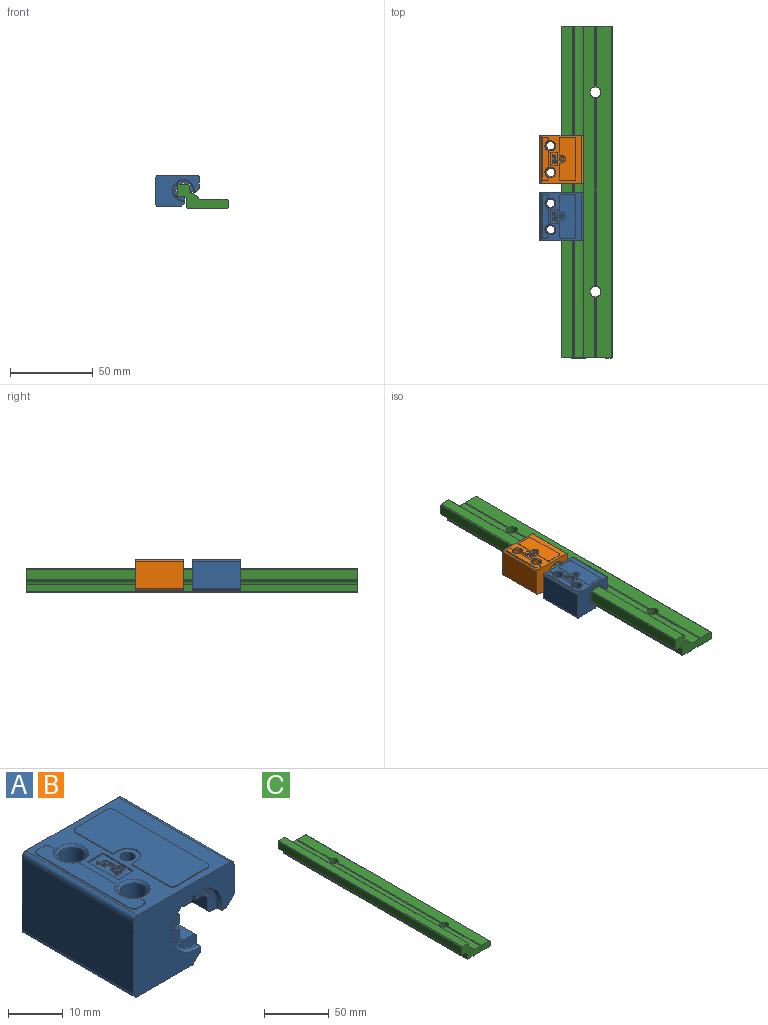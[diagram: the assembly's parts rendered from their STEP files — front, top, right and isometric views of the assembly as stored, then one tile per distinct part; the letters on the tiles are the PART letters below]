
ASSEMBLY  parts=3 mates=2
PART A: 216 faces, bbox 26.3x29.3x18.8 mm
  f0: plane 0.15x0.14mm, normal (0,0,1), area 0mm2, adj f1,f2,f3,f4
  f1: plane 0.15x0.15mm, normal (0,1,0), area 0mm2, adj f0,f2,f4,f5
  f2: plane 0.15x0.06mm, normal (1,0,0), area 0mm2, adj f0,f1,f3,f5
  f3: cylinder r=0.07mm len=0.15mm, axis (0,0,1), area 0mm2, adj f0,f2,f4,f5
  f4: plane 0.15x0.06mm, normal (-1,0,0), area 0mm2, adj f0,f1,f3,f5
  f5: plane 0.35x0.16mm, normal (0,0,1), area 0mm2, adj f1,f2,f3,f4,f6,f7,f8,f9
  f6: plane 0.18x0.15mm, normal (0,1,0), area 0mm2, adj f5,f7,f15,f16
  f7: plane 0.15x0.01mm, normal (1,0,0), area 0mm2, adj f5,f6,f8,f16
  f8: plane 0.35x0.15mm, normal (0,-1,0), area 0.1mm2, adj f5,f7,f9,f16
  f9: plane 0.15x0.08mm, normal (-1,0,0), area 0mm2, adj f5,f8,f10,f16
  f10: cylinder r=0.09mm len=0.18mm, axis (0,0,-1), area 0mm2, adj f5,f9,f11,f16
  f11: plane 0.15x0.01mm, normal (1,0,0), area 0mm2, adj f5,f10,f12,f16
  f12: plane 0.18x0.15mm, normal (-0.5,0.87,0), area 0mm2, adj f5,f11,f13,f16
  f13: plane 0.15x0.01mm, normal (1,0,0), area 0mm2, adj f5,f12,f14,f16
  f14: plane 0.18x0.15mm, normal (0.5,-0.87,0), area 0mm2, adj f5,f13,f15,f16
  f15: plane 0.15x0.04mm, normal (1,0,0), area 0mm2, adj f5,f6,f14,f16
  f16: plane 0.51x0.51mm, normal (0,0,1), area 0.2mm2, adj f6,f7,f8,f9,f10,f11,f12,f13
  f17: plane 1.38x0.63mm, normal (0,0,1), area 0.6mm2, adj f21,f22
  f18: plane 1.36x0.62mm, normal (0,0,1), area 0.6mm2, adj f23,f24
  f19: plane 1.37x0.74mm, normal (0,0,1), area 0.8mm2, adj f25,f26
  f20: cylinder r=0.25mm len=0.5mm, axis (0,0,1), area 0.2mm2, adj f16,f59
  f21: cylinder r=0.68mm len=1.35mm, axis (0,0,1), area 0.3mm2, adj f17,f22,f60
  f22: plane 1.35x0.15mm, normal (1,0,0), area 0.2mm2, adj f17,f21,f60
  f23: cylinder r=0.68mm len=1.34mm, axis (0,0,1), area 0.3mm2, adj f18,f24,f60
  f24: plane 1.34x0.15mm, normal (1,0,0), area 0.2mm2, adj f18,f23,f60
  f25: plane 1.35x0.15mm, normal (-1,0,0), area 0.2mm2, adj f19,f26,f60
  f26: cylinder r=0.68mm len=1.35mm, axis (0,0,1), area 0.3mm2, adj f19,f25,f60
  f27: plane 0.35x0.15mm, normal (0,1,0), area 0mm2, adj f29,f74,f79
  f28: plane 0.35x0.15mm, normal (0,-1,0), area 0mm2, adj f30,f74,f80
  f29: cylinder r=6mm len=12mm, axis (0,1,0), area 4.1mm2, adj f27,f74,f79,f85
  f30: cylinder r=6mm len=12mm, axis (0,1,0), area 4.1mm2, adj f28,f74,f80,f87
  f31: plane 27x2.99mm, normal (0,0,1), area 80.7mm2, adj f32,f85,f86,f87
  f32: plane 27x0.46mm, normal (-0.71,0,0.71), area 17.5mm2, adj f31,f33,f85,f87
  f33: cylinder r=0.3mm len=27mm, axis (0,-1,0), area 12.7mm2, adj f32,f34,f85,f87
  f34: plane 27x0.64mm, normal (0.71,0,0.71), area 24.3mm2, adj f33,f35,f85,f87
  f35: cylinder r=0.3mm len=27mm, axis (0,-1,0), area 12.7mm2, adj f34,f36,f85,f87
  f36: plane 27x0.46mm, normal (0.71,0,-0.71), area 17.5mm2, adj f35,f37,f85,f87
  f37: plane 27x2.19mm, normal (1,0,0), area 59.1mm2, adj f36,f38,f85,f87
  f38: plane 27x0.75mm, normal (0,0,1), area 20.2mm2, adj f37,f39,f85,f87
  f39: cylinder r=0.5mm len=27mm, axis (0,-1,0), area 42.4mm2, adj f38,f40,f85,f87
  f40: plane 27x0.75mm, normal (0,0,-1), area 20.2mm2, adj f39,f41,f85,f87
  f41: plane 27x2.19mm, normal (1,0,0), area 59.1mm2, adj f40,f42,f85,f87
  f42: plane 27x0.46mm, normal (0.71,0,0.71), area 17.5mm2, adj f41,f43,f85,f87
  f43: cylinder r=0.3mm len=27mm, axis (0,-1,0), area 12.7mm2, adj f42,f44,f85,f87
  f44: plane 27x0.64mm, normal (0.71,0,-0.71), area 24.3mm2, adj f43,f45,f85,f87
  f45: cylinder r=0.3mm len=27mm, axis (0,-1,0), area 12.7mm2, adj f44,f46,f85,f87
  f46: plane 27x0.46mm, normal (-0.71,0,-0.71), area 17.5mm2, adj f45,f47,f85,f87
  f47: plane 27x2.19mm, normal (0,0,-1), area 59.1mm2, adj f46,f48,f85,f87
  f48: plane 27x0.75mm, normal (1,0,0), area 20.2mm2, adj f47,f49,f85,f87
  f49: cylinder r=0.5mm len=27mm, axis (0,-1,0), area 42.4mm2, adj f48,f50,f85,f87
  f50: plane 27x0.75mm, normal (-1,0,0), area 20.2mm2, adj f49,f51,f85,f87
  f51: plane 27x2.19mm, normal (0,0,-1), area 59.1mm2, adj f50,f52,f85,f87
  f52: plane 27x0.46mm, normal (0.71,0,-0.71), area 17.5mm2, adj f51,f53,f85,f87
  f53: cylinder r=0.3mm len=27mm, axis (0,-1,0), area 12.7mm2, adj f52,f54,f85,f87
  f54: plane 27x0.64mm, normal (-0.71,0,-0.71), area 24.3mm2, adj f53,f55,f85,f87
  f55: cylinder r=0.3mm len=27mm, axis (0,-1,0), area 12.7mm2, adj f54,f56,f85,f87
  f56: plane 27x0.46mm, normal (-0.71,0,0.71), area 17.5mm2, adj f55,f57,f85,f87
  f57: plane 27x2.99mm, normal (-1,0,0), area 80.7mm2, adj f56,f58,f85,f87
  f58: plane 27x0.5mm, normal (-0.71,0,-0.71), area 19.1mm2, adj f57,f74,f85,f87
  f59: plane 0.56x0.56mm, normal (0,0,1), area 0mm2, adj f20,f91
  f60: plane 5.04x2.57mm, normal (0,0,1), area 3.1mm2, adj f21,f22,f23,f24,f25,f26,f92,f93
  f61: plane 0.2x0.2mm, normal (0,0,1), area 0mm2, adj f149
  f62: plane 3x0.5mm, normal (-0.71,0,0.71), area 2.1mm2, adj f63,f90,f150,f151
  f63: cylinder r=6mm len=3mm, axis (0,1,0), area 4.5mm2, adj f62,f64,f150,f151
  f64: plane 3x0.5mm, normal (0.71,0,-0.71), area 2.1mm2, adj f63,f65,f150,f151
  f65: cylinder r=6.7mm len=8.36mm, axis (0,1,0), area 27.1mm2, adj f64,f66,f150,f151
  f66: plane 3x0.5mm, normal (0.71,0,0.71), area 2.1mm2, adj f65,f67,f150,f151
  f67: cylinder r=6mm len=3mm, axis (0,1,0), area 4.5mm2, adj f66,f68,f150,f151
  f68: plane 3x0.5mm, normal (-0.71,0,-0.71), area 2.1mm2, adj f67,f69,f150,f151
  f69: cylinder r=6.7mm len=8.36mm, axis (0,1,0), area 27.1mm2, adj f68,f70,f150,f151
  f70: plane 3x0.5mm, normal (0.71,0,-0.71), area 2.1mm2, adj f69,f71,f150,f151
  f71: cylinder r=6mm len=3mm, axis (0,1,0), area 4.5mm2, adj f70,f72,f150,f151
  f72: plane 3x0.5mm, normal (-0.71,0,0.71), area 2.1mm2, adj f71,f73,f150,f151
  f73: cylinder r=6.7mm len=4.98mm, axis (0,1,0), area 15.9mm2, adj f72,f74,f150,f151
  f74: plane 27x2.4mm, normal (0,0,-1), area 47.9mm2, adj f27,f28,f29,f30,f58,f73,f85,f87
  f75: cylinder r=6mm len=12mm, axis (0,1,0), area 14.4mm2, adj f76,f79,f85,f154,f155
  f76: plane 12.51x0.31mm, normal (0,0,1), area 3.8mm2, adj f75,f82,f83,f84,f155
  f77: plane 12.51x0.31mm, normal (0,0,1), area 3.8mm2, adj f78,f81,f88,f89,f156
  f78: cylinder r=6mm len=12mm, axis (0,1,0), area 14.4mm2, adj f77,f80,f87,f156,f157
  f79: cylinder r=0.5mm len=13mm, axis (0,-1,0), area 10.5mm2, adj f27,f29,f75,f151,f154,f158,f175
  f80: cylinder r=0.5mm len=13mm, axis (0,-1,0), area 10.5mm2, adj f28,f30,f78,f150,f157,f158,f177
  f81: cylinder r=0.5mm len=13mm, axis (0,-1,0), area 10mm2, adj f77,f89,f156,f165,f177
  f82: cylinder r=0.5mm len=13mm, axis (0,-1,0), area 10mm2, adj f76,f83,f155,f165,f175
  f83: plane 0.8x0.56mm, normal (0,1,0), area 0.1mm2, adj f76,f82,f84,f165
  f84: cylinder r=6mm len=12mm, axis (0,1,0), area 9.6mm2, adj f76,f83,f85,f165
  f85: plane 12.02x12.01mm, normal (0,1,0), area 41.2mm2, adj f29,f31,f32,f33,f34,f35,f36,f37
  f86: plane 27x0.5mm, normal (0.71,0,0.71), area 19.1mm2, adj f31,f85,f87,f165
  f87: plane 12.02x12.01mm, normal (0,-1,0), area 41.2mm2, adj f30,f31,f32,f33,f34,f35,f36,f37
  f88: cylinder r=6mm len=12mm, axis (0,1,0), area 9.6mm2, adj f77,f87,f89,f165
  f89: plane 0.8x0.56mm, normal (0,-1,0), area 0.1mm2, adj f77,f81,f88,f165
  f90: cylinder r=6.7mm len=4.98mm, axis (0,1,0), area 15.9mm2, adj f62,f150,f151,f165
  f91: cylinder r=0.28mm len=0.55mm, axis (0,0,-1), area 0.3mm2, adj f59,f167
  f92: plane 0.24x0.15mm, normal (1,0,0), area 0mm2, adj f60,f93,f148,f167
  f93: cylinder r=0.45mm len=0.75mm, axis (0,0,-1), area 0.2mm2, adj f60,f92,f94,f167
  f94: plane 0.4x0.15mm, normal (1,0,0), area 0.1mm2, adj f60,f93,f95,f167
  f95: cylinder r=0.35mm len=0.35mm, axis (0,0,-1), area 0.1mm2, adj f60,f94,f96,f167
  f96: plane 0.15x0.15mm, normal (-1,0,0), area 0mm2, adj f60,f95,f97,f167
  f97: cylinder r=0.26mm len=0.25mm, axis (0,0,1), area 0.1mm2, adj f60,f96,f98,f167
  f98: plane 0.35x0.15mm, normal (-1,0,0), area 0.1mm2, adj f60,f97,f99,f167
  f99: cylinder r=0.3mm len=0.6mm, axis (0,0,1), area 0.1mm2, adj f60,f98,f100,f167
  f100: plane 0.78x0.15mm, normal (1,0,0), area 0.1mm2, adj f60,f99,f101,f167
  f101: plane 0.75x0.15mm, normal (0,1,0), area 0.1mm2, adj f60,f100,f102,f167
  f102: plane 0.15x0.15mm, normal (1,0,0), area 0mm2, adj f60,f101,f103,f167
  f103: plane 0.35x0.15mm, normal (0,-1,0), area 0.1mm2, adj f60,f102,f104,f167
  f104: cylinder r=0.8mm len=1.5mm, axis (0,0,-1), area 0.3mm2, adj f60,f103,f105,f167
  f105: plane 0.15x0.03mm, normal (1,0,0), area 0mm2, adj f60,f104,f106,f167
  f106: plane 0.75x0.15mm, normal (0,1,0), area 0.1mm2, adj f60,f105,f107,f167
  f107: cylinder r=0.82mm len=1.65mm, axis (0,0,-1), area 0.4mm2, adj f60,f106,f108,f167
  f108: plane 0.15x0.15mm, normal (-1,0,0), area 0mm2, adj f60,f107,f109,f167
  f109: cylinder r=0.68mm len=1.35mm, axis (0,0,1), area 0.3mm2, adj f60,f108,f110,f167
  f110: plane 0.4x0.15mm, normal (0,-1,0), area 0.1mm2, adj f60,f109,f111,f167
  f111: cylinder r=0.79mm len=1.5mm, axis (0,0,-1), area 0.3mm2, adj f60,f110,f112,f167
  f112: plane 0.15x0.03mm, normal (1,0,0), area 0mm2, adj f60,f111,f113,f167
  f113: plane 0.75x0.15mm, normal (0,1,0), area 0.1mm2, adj f60,f112,f114,f167
  f114: plane 0.15x0.15mm, normal (1,0,0), area 0mm2, adj f60,f113,f115,f167
  f115: plane 0.75x0.15mm, normal (0,-1,0), area 0.1mm2, adj f60,f114,f116,f167
  f116: plane 0.15x0.15mm, normal (1,0,0), area 0mm2, adj f60,f115,f117,f167
  f117: plane 0.15x0.03mm, normal (0,-1,0), area 0mm2, adj f60,f116,f118,f167
  f118: plane 0.15x0.15mm, normal (-1,0,0), area 0mm2, adj f60,f117,f119,f167
  f119: plane 0.9x0.15mm, normal (0,-1,0), area 0.1mm2, adj f60,f118,f120,f167
  f120: plane 0.15x0.15mm, normal (-1,0,0), area 0mm2, adj f60,f119,f121,f167
  f121: plane 0.88x0.15mm, normal (0,1,0), area 0.1mm2, adj f60,f120,f122,f167
  f122: plane 0.15x0.03mm, normal (-1,0,0), area 0mm2, adj f60,f121,f123,f167
  f123: cylinder r=0.81mm len=1.51mm, axis (0,0,-1), area 0.3mm2, adj f60,f122,f124,f167
  f124: plane 0.35x0.15mm, normal (0,-1,0), area 0.1mm2, adj f60,f123,f125,f167
  f125: plane 0.15x0.15mm, normal (-1,0,0), area 0mm2, adj f60,f124,f126,f167
  f126: plane 0.88x0.15mm, normal (0,1,0), area 0.1mm2, adj f60,f125,f127,f167
  f127: plane 0.15x0.03mm, normal (-1,0,0), area 0mm2, adj f60,f126,f128,f167
  f128: plane 0.88x0.15mm, normal (0,-1,0), area 0.1mm2, adj f60,f127,f129,f167
  f129: plane 0.15x0.15mm, normal (-1,0,0), area 0mm2, adj f60,f128,f130,f167
  f130: plane 0.88x0.15mm, normal (0,1,0), area 0.1mm2, adj f60,f129,f131,f167
  f131: plane 1.35x0.15mm, normal (-1,0,0), area 0.2mm2, adj f60,f130,f132,f167
  f132: cylinder r=0.68mm len=0.15mm, axis (0,0,1), area 0mm2, adj f60,f131,f133,f167
  f133: plane 0.83x0.15mm, normal (0,-1,0), area 0.1mm2, adj f60,f132,f134,f167
  f134: plane 0.15x0.15mm, normal (-1,0,0), area 0mm2, adj f60,f133,f135,f167
  f135: plane 0.88x0.15mm, normal (0,1,0), area 0.1mm2, adj f60,f134,f136,f167
  f136: plane 0.3x0.15mm, normal (-1,0,0), area 0mm2, adj f60,f135,f137,f167
  f137: cylinder r=0.49mm len=0.43mm, axis (0,0,-1), area 0.1mm2, adj f60,f136,f138,f167
  f138: cylinder r=0.4mm len=0.45mm, axis (0,0,-1), area 0.1mm2, adj f60,f137,f139,f167
  f139: plane 0.38x0.15mm, normal (-1,0,0), area 0.1mm2, adj f60,f138,f140,f167
  f140: cylinder r=0.35mm len=0.35mm, axis (0,0,-1), area 0.1mm2, adj f60,f139,f141,f167
  f141: plane 0.15x0.15mm, normal (1,0,0), area 0mm2, adj f60,f140,f142,f167
  f142: cylinder r=0.26mm len=0.25mm, axis (0,0,1), area 0.1mm2, adj f60,f141,f143,f167
  f143: plane 0.28x0.15mm, normal (1,0,0), area 0mm2, adj f60,f142,f144,f167
  f144: cylinder r=0.3mm len=0.6mm, axis (0,0,1), area 0.1mm2, adj f60,f143,f145,f167
  f145: plane 0.28x0.15mm, normal (-1,0,0), area 0mm2, adj f60,f144,f146,f167
  f146: cylinder r=0.45mm len=0.31mm, axis (0,0,-1), area 0.1mm2, adj f60,f145,f147,f167
  f147: plane 0.26x0.15mm, normal (-1,0,0), area 0mm2, adj f60,f146,f148,f167
  f148: plane 0.15x0.03mm, normal (0,1,0), area 0mm2, adj f60,f92,f147,f167
  f149: cylinder r=0.1mm len=0.2mm, axis (0,0,-1), area 0.1mm2, adj f61,f167
  f150: plane 14.13x14.11mm, normal (0,1,0), area 10mm2, adj f62,f63,f64,f65,f66,f67,f68,f69
  f151: plane 14.13x14.11mm, normal (0,-1,0), area 10mm2, adj f62,f63,f64,f65,f66,f67,f68,f69
  f152: cone r=3mm half-angle=45deg, axis (0,0,-1), area 12.2mm2, adj f153,f169
  f153: plane 9.64x9.64mm, normal (0,0,-1), area 42.6mm2, adj f152,f174
  f154: cone r=6mm half-angle=45deg, axis (0,1,0), area 0.6mm2, adj f75,f79,f155,f175
  f155: cone r=6mm half-angle=45deg, axis (0,1,0), area 21.3mm2, adj f75,f76,f82,f154,f175
  f156: cone r=6.5mm half-angle=45deg, axis (0,-1,0), area 7.4mm2, adj f77,f78,f81,f157,f177
  f157: cone r=6.5mm half-angle=45deg, axis (0,-1,0), area 14.5mm2, adj f78,f80,f156,f177
  f158: plane 29x0.81mm, normal (0,0,-1), area 22.5mm2, adj f79,f80,f150,f151,f159,f168,f175,f177
  f159: cylinder r=0.5mm len=29mm, axis (0,-1,0), area 11.4mm2, adj f158,f160,f175,f177
  f160: plane 29x1.71mm, normal (0.71,0,-0.71), area 70mm2, adj f159,f161,f175,f177
  f161: cylinder r=0.5mm len=29mm, axis (0,-1,0), area 11.4mm2, adj f160,f166,f175,f177
  f162: plane 29x16.3mm, normal (-1,0,0), area 472.7mm2, adj f173,f175,f176,f177
  f163: plane 29x1.71mm, normal (0.71,0,-0.71), area 70mm2, adj f164,f172,f175,f177
  f164: cylinder r=0.5mm len=29mm, axis (0,-1,0), area 11.4mm2, adj f163,f165,f175,f177
  f165: plane 29x3.04mm, normal (1,0,0), area 69.9mm2, adj f81,f82,f83,f84,f85,f86,f87,f88
  f166: plane 29x6.59mm, normal (1,0,0), area 191.2mm2, adj f161,f175,f177,f178
  f167: plane 8x4mm, normal (0,0,1), area 26.6mm2, adj f91,f92,f93,f94,f95,f96,f97,f98
  f168: cylinder r=6.9mm len=13.8mm, axis (0,1,0), area 95.6mm2, adj f150,f151,f158,f165,f183
  f169: cylinder r=2.5mm len=12.3mm, axis (0,0,1), area 193.2mm2, adj f152,f184
  f170: plane 26.12x3.62mm, normal (0,0,1), area 72mm2, adj f185,f186,f187,f188,f189,f190,f191,f192
  f171: plane 26.07x10.07mm, normal (0,0,1), area 243.4mm2, adj f197,f198,f199,f200,f201,f202,f203,f204
  f172: cylinder r=0.5mm len=29mm, axis (0,-1,0), area 11.4mm2, adj f163,f175,f177,f209
  f173: cylinder r=1mm len=29mm, axis (0,-1,0), area 45.6mm2, adj f162,f175,f177,f209
  f174: cylinder r=4.75mm len=9.5mm, axis (0,0,1), area 149.2mm2, adj f153,f209
  f175: plane 26.03x18.33mm, normal (0,1,0), area 286.8mm2, adj f79,f82,f154,f155,f158,f159,f160,f161
  f176: cylinder r=1mm len=29mm, axis (0,-1,0), area 45.6mm2, adj f162,f175,f177,f210
  f177: plane 26.03x18.33mm, normal (0,-1,0), area 286.7mm2, adj f80,f81,f156,f157,f158,f159,f160,f161
  f178: cylinder r=1mm len=29mm, axis (0,-1,0), area 45.6mm2, adj f166,f175,f177,f210
  f179: plane 4x0.3mm, normal (0,1,0), area 1.2mm2, adj f167,f180,f182,f210
  f180: plane 8x0.3mm, normal (1,0,0), area 2.4mm2, adj f167,f179,f181,f210
  f181: plane 4x0.3mm, normal (0,-1,0), area 1.2mm2, adj f167,f180,f182,f210
  f182: plane 8x0.3mm, normal (-1,0,0), area 2.4mm2, adj f167,f179,f181,f210
  f183: cylinder r=1.4mm len=4.05mm, axis (0,0,1), area 27.7mm2, adj f168,f210
  f184: cone r=2.5mm half-angle=45deg, axis (0,0,1), area 12.2mm2, adj f169,f210
  f185: cylinder r=3.5mm len=6.32mm, axis (0,0,-1), area 1.6mm2, adj f170,f186,f196,f210
  f186: plane 0.84x0.2mm, normal (1,0,0), area 0.2mm2, adj f170,f185,f187,f210
  f187: cylinder r=1mm len=1mm, axis (0,0,1), area 0.3mm2, adj f170,f186,f188,f210
  f188: plane 1.5x0.2mm, normal (0,-1,0), area 0.3mm2, adj f170,f187,f189,f210
  f189: cylinder r=1mm len=1mm, axis (0,0,1), area 0.3mm2, adj f170,f188,f190,f210
  f190: plane 24x0.2mm, normal (-1,0,0), area 4.8mm2, adj f170,f189,f191,f210
  f191: cylinder r=1mm len=1mm, axis (0,0,1), area 0.3mm2, adj f170,f190,f192,f210
  f192: plane 1.5x0.2mm, normal (0,1,0), area 0.3mm2, adj f170,f191,f193,f210
  f193: cylinder r=1mm len=1mm, axis (0,0,1), area 0.3mm2, adj f170,f192,f194,f210
  f194: plane 0.84x0.2mm, normal (1,0,0), area 0.2mm2, adj f170,f193,f195,f210
  f195: cylinder r=3.5mm len=6.32mm, axis (0,0,-1), area 1.6mm2, adj f170,f194,f196,f210
  f196: plane 9.68x0.2mm, normal (1,0,0), area 1.9mm2, adj f170,f185,f195,f210
  f197: cylinder r=1mm len=1mm, axis (0,0,1), area 0.3mm2, adj f171,f198,f208,f210
  f198: plane 8x0.2mm, normal (0,-1,0), area 1.6mm2, adj f171,f197,f199,f210
  f199: cylinder r=1mm len=1mm, axis (0,0,1), area 0.3mm2, adj f171,f198,f200,f210
  f200: plane 9.6x0.2mm, normal (-1,0,0), area 1.9mm2, adj f171,f199,f201,f210
  f201: plane 1.4x0.2mm, normal (0,1,0), area 0.3mm2, adj f171,f200,f202,f210
  f202: cylinder r=2.4mm len=4.8mm, axis (0,0,-1), area 1.5mm2, adj f171,f201,f203,f210
  f203: plane 1.4x0.2mm, normal (0,-1,0), area 0.3mm2, adj f171,f202,f204,f210
  f204: plane 9.6x0.2mm, normal (-1,0,0), area 1.9mm2, adj f171,f203,f205,f210
  f205: cylinder r=1mm len=1mm, axis (0,0,1), area 0.3mm2, adj f171,f204,f206,f210
  f206: plane 8x0.2mm, normal (0,1,0), area 1.6mm2, adj f171,f205,f207,f210
  f207: cylinder r=1mm len=1mm, axis (0,0,1), area 0.3mm2, adj f171,f206,f208,f210
  f208: plane 24x0.2mm, normal (1,0,0), area 4.8mm2, adj f171,f197,f207,f210
  f209: plane 29.14x14.23mm, normal (0,0,-1), area 266.9mm2, adj f172,f173,f174,f175,f177,f211
  f210: plane 29.08x24.08mm, normal (0,0,1), area 285.9mm2, adj f175,f176,f177,f178,f179,f180,f181,f182
  f211: cylinder r=4.75mm len=9.5mm, axis (0,0,1), area 149.2mm2, adj f209,f213
  f212: cone r=2.5mm half-angle=45deg, axis (0,0,1), area 12.2mm2, adj f210,f214
  f213: plane 9.58x9.58mm, normal (0,0,-1), area 42.6mm2, adj f211,f215
  f214: cylinder r=2.5mm len=12.3mm, axis (0,0,1), area 193.2mm2, adj f212,f215
  f215: cone r=3mm half-angle=45deg, axis (0,0,-1), area 12.2mm2, adj f213,f214
PART B: same geometry as A
PART C: 32 faces, bbox 30.8x200.1x14.8 mm
  f0: plane 200x4.5mm, normal (1,0,0), area 900mm2, adj f13,f15,f21,f23
  f1: plane 200x0.5mm, normal (0.71,0,0.71), area 141.4mm2, adj f2,f18,f21,f23
  f2: plane 200x4.2mm, normal (1,0,0), area 840mm2, adj f1,f3,f21,f23
  f3: plane 200x0.5mm, normal (0.71,0,0.71), area 141.4mm2, adj f2,f4,f21,f23
  f4: plane 200x6.5mm, normal (0,0,1), area 1300mm2, adj f3,f5,f21,f23
  f5: plane 200x0.5mm, normal (-0.71,0,0.71), area 141.4mm2, adj f4,f6,f21,f23
  f6: plane 200x6.5mm, normal (-1,0,0), area 1300mm2, adj f5,f7,f21,f23
  f7: plane 200x0.5mm, normal (-0.71,0,-0.71), area 141.4mm2, adj f6,f8,f21,f23
  f8: plane 200x4.2mm, normal (0,0,-1), area 840mm2, adj f7,f9,f21,f23
  f9: cylinder r=3.03mm len=200mm, axis (0,1,0), area 505.7mm2, adj f8,f10,f21,f23
  f10: plane 200x4.41mm, normal (-1,0,0), area 881.5mm2, adj f9,f11,f21,f23
  f11: plane 200x0.5mm, normal (-0.71,0,-0.71), area 141.4mm2, adj f10,f14,f21,f23
  f12: plane 200x3.5mm, normal (0,0,-1), area 700mm2, adj f13,f21,f22,f23
  f13: plane 200x0.5mm, normal (0.71,0,-0.71), area 141.4mm2, adj f0,f12,f21,f23
  f14: plane 200x8.5mm, normal (0,0,-1), area 1700mm2, adj f11,f21,f23,f24
  f15: plane 200x0.5mm, normal (0.71,0,0.71), area 141.4mm2, adj f0,f21,f23,f26
  f16: plane 36.74x0.5mm, normal (-0.5,0,0.87), area 21.2mm2, adj f17,f21,f25,f26
  f17: plane 36.74x0.5mm, normal (0.5,0,0.87), area 21.2mm2, adj f16,f21,f25,f29
  f18: cylinder r=7mm len=200mm, axis (0,-1,0), area 1383.2mm2, adj f1,f21,f23,f29
  f19: plane 36.74x0.5mm, normal (0.5,0,0.87), area 21.2mm2, adj f20,f23,f29,f31
  f20: plane 36.74x0.5mm, normal (-0.5,0,0.87), area 21.2mm2, adj f19,f23,f26,f31
  f21: plane 30.7x14.65mm, normal (0,1,0), area 210.5mm2, adj f0,f1,f2,f3,f4,f5,f6,f7
  f22: plane 200x0.2mm, normal (-0.71,0,-0.71), area 56.6mm2, adj f12,f21,f23,f30
  f23: plane 30.7x14.65mm, normal (0,-1,0), area 210.5mm2, adj f0,f1,f2,f3,f4,f5,f6,f7
  f24: plane 200x0.2mm, normal (0.71,0,-0.71), area 56.6mm2, adj f14,f21,f23,f30
  f25: cylinder r=3.3mm len=6.6mm, axis (0,0,1), area 109.6mm2, adj f16,f17,f26,f27,f28,f29,f30
  f26: plane 200.12x9.12mm, normal (0,0,1), area 1772.4mm2, adj f15,f16,f20,f21,f23,f25,f27,f31
  f27: plane 113.48x0.5mm, normal (-0.5,0,0.87), area 65.5mm2, adj f25,f26,f28,f31
  f28: plane 113.48x0.5mm, normal (0.5,0,0.87), area 65.5mm2, adj f25,f27,f29,f31
  f29: plane 200.12x6.98mm, normal (0,0,1), area 1345.4mm2, adj f17,f18,f19,f21,f23,f25,f28,f31
  f30: plane 200.09x11.69mm, normal (0,0,-1), area 2251.6mm2, adj f21,f22,f23,f24,f25,f31
  f31: cylinder r=3.3mm len=6.6mm, axis (0,0,1), area 109.6mm2, adj f19,f20,f26,f27,f28,f29,f30
PLACE A t=(-25.39,-27.4,18.29)mm
PLACE B t=(-25.38,7.15,18.27)mm
PLACE C t=(1.57,-98.15,7.37)mm fixed
MATE slider A.f177 <-> C.f23  axis (0,-1,0) through (-32.33,-27.4,18.87)mm
MATE slider B.f175 <-> C.f21  axis (0,1,0) through (-40.88,36.15,27.07)mm
